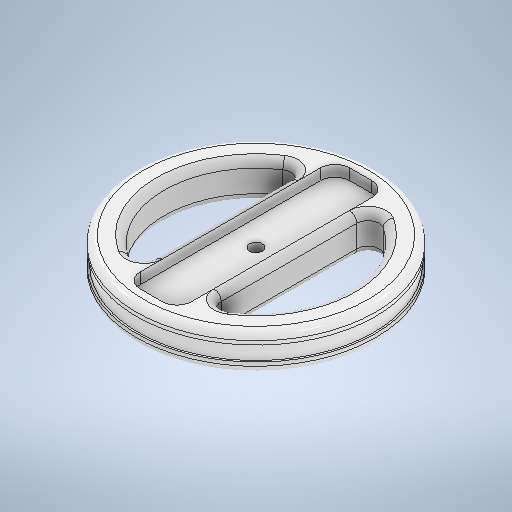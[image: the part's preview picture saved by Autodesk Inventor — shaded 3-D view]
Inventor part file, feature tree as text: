
AUTODESK INVENTOR PART (.ipt)
format: ipt  version: 2025 (Build 290162000, 162)  size: 795,136 bytes
history: native  units: mm
features: fillet x4, sketch x4, extrude x3, other x1
ambient origin geometry x8: Origin, YZ Plane, XZ Plane, XY Plane, X Axis, Y Axis, Z Axis, Center Point
bodies: Solide1 (feature_tree)
feature tree (12):
  other  "Révolution1"
  extrude  "Extrusion1"  Depth=32.5mm
  fillet  "Congé1"  Radius=10.0mm
  extrude  "Extrusion2"  Depth=3.0mm
  fillet  "Congé2"  Radius=0.5mm
  extrude  "Extrusion3"  TaperAngle=90.0deg  [1 undecoded]
  fillet  "Congé3"  Radius=14.0mm
  fillet  "Congé4"  Radius=57.0mm
  sketch  "Esquisse2"
  sketch  "Esquisse3"
  sketch  "Esquisse4"
  sketch  "Esquisse5"
note: 1 required parameter value undecoded (feature->parameter linkage not recoverable at this tier; creation-order binding heuristic only, values carry confidence <= 0.55)
